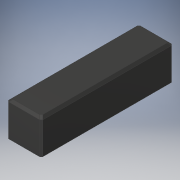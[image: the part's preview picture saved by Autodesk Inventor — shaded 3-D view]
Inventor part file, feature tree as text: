
AUTODESK INVENTOR PART (.ipt)
format: ipt  version: 2019 (Build 230136000, 136)  size: 155,648 bytes
history: native  units: mm
features: chamfer x3, extrude x2, sketch x2
ambient origin geometry x8: Origin, YZ Plane, XZ Plane, XY Plane, X Axis, Y Axis, Z Axis, Center Point
bodies: Solid1 (feature_tree)
feature tree (7):
  extrude  "Extrusion1"  Depth=22.5mm
  extrude  "Extrusion5"  Depth=2.0mm
  chamfer  "Chamfer1"  Distance=2.0mm
  chamfer  "Chamfer2"  Distance=20.5mm
  chamfer  "Chamfer3"  Distance=20.5mm
  sketch  "Sketch1"  dims[d0=22.5mm d1=22.5mm]
  sketch  "Sketch6"  dims[d2=20.5mm d3=2.0mm d4=2.0mm d5=20.5mm d6=20.5mm d7=2.0mm d8=2.0mm d9=20.5mm d10=18.5mm d11=18.5mm d12=86.75mm d13=0.0mm d28=20.5mm d29=2.0mm d30=2.0mm d31=84.75mm d32=20.5mm d33=2.0mm d34=2.0mm d35=84.75mm d36=18.5mm d37=82.75mm d38=20.5mm d39=0.0mm d40=1.5mm d41=2.0mm d42=45.0deg d43=1.0mm d44=2.0mm d45=45.0deg d46=0.8165mm d47=2.0mm d48=45.0deg]
